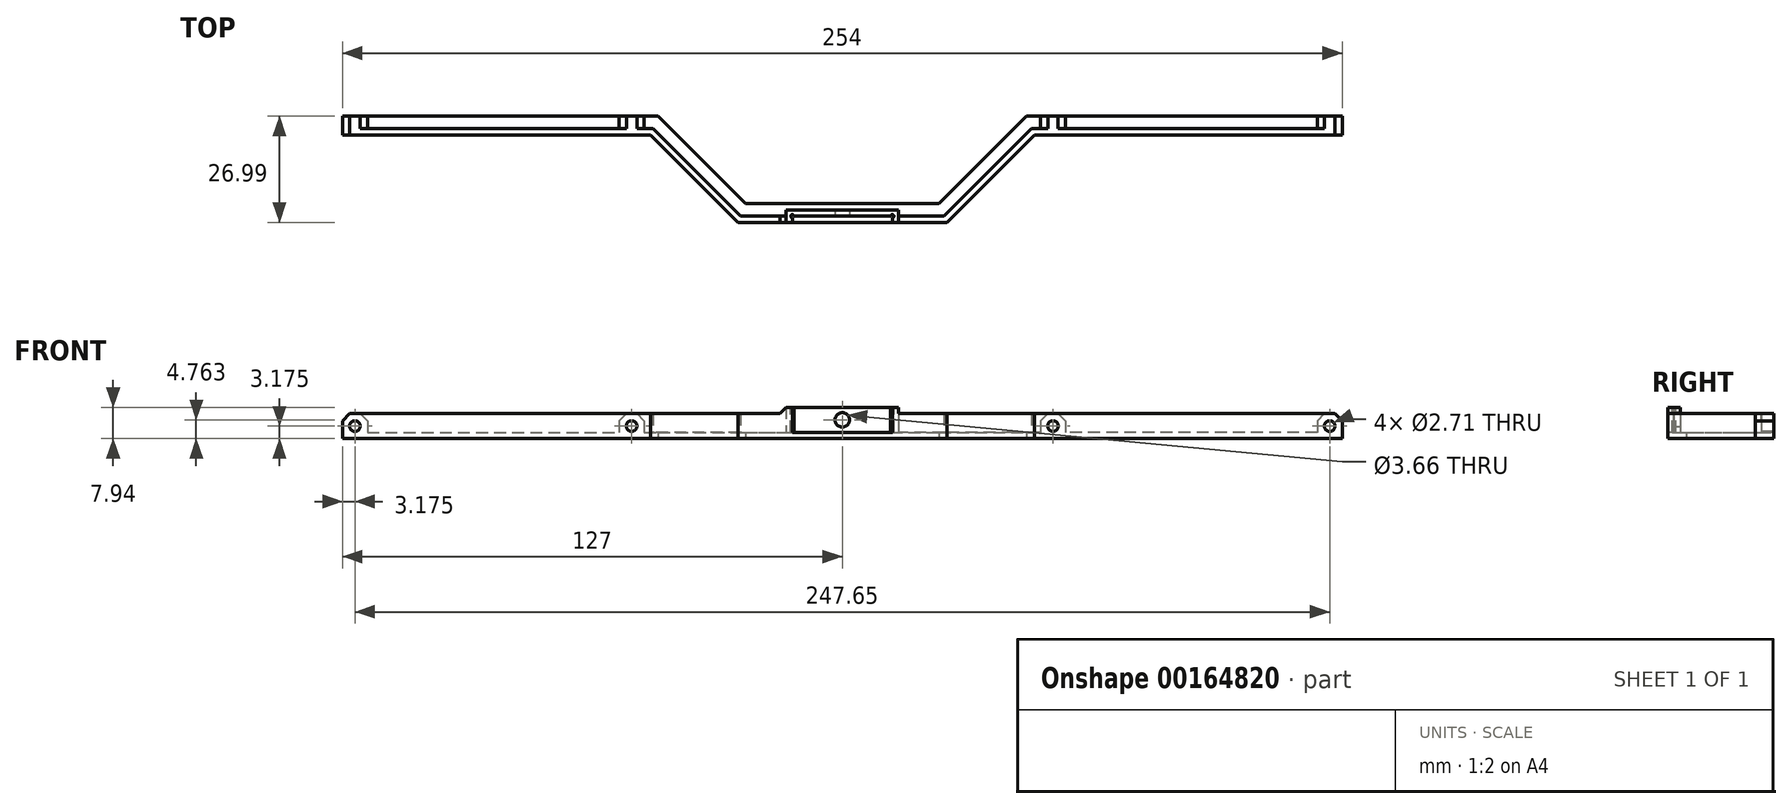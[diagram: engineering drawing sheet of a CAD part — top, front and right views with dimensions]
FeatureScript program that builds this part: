
annotation { "Feature Type Name" : "Feature", "Feature Type Description" : "" }
export const myFeature = defineFeature(function(context is Context, id is Id, definition is map)
    precondition{}
    {
        {
            var Q0;
            Q0=qCreatedBy(makeId("Top.planeOp"),FACE);
            var sketch = newSketch(context, id + "F0", { "sketchPlane" : qUnion([Q0])});
            skLineSegment(sketch, "E0", {"start": v(-127, 22.22) * mm, "end": v(-46.78, 22.22) * mm});
            skLineSegment(sketch, "E1", {"start": v(-46.78, 22.23) * mm, "end": v(-24.56, 0) * mm});
            skLineSegment(sketch, "E2", {"start": v(-24.56, 0) * mm, "end": v(24.56, 0) * mm});
            skLineSegment(sketch, "E3", {"start": v(24.56, 0) * mm, "end": v(46.78, 22.23) * mm});
            skLineSegment(sketch, "E4", {"start": v(46.78, 22.22) * mm, "end": v(127, 22.22) * mm});
            skLineSegment(sketch, "E5", {"start": v(-127, 22.23) * mm, "end": v(-127, 17.46) * mm});
            skLineSegment(sketch, "E6", {"start": v(-127, 17.46) * mm, "end": v(-48.76, 17.46) * mm});
            skLineSegment(sketch, "E7", {"start": v(-48.76, 17.46) * mm, "end": v(-26.53, -4.76) * mm});
            skLineSegment(sketch, "E8", {"start": v(-26.53, -4.76) * mm, "end": v(26.53, -4.76) * mm});
            skLineSegment(sketch, "E9", {"start": v(26.53, -4.76) * mm, "end": v(48.76, 17.46) * mm});
            skLineSegment(sketch, "E10", {"start": v(48.76, 17.46) * mm, "end": v(127, 17.46) * mm});
            skLineSegment(sketch, "E11", {"start": v(127, 17.46) * mm, "end": v(127, 22.23) * mm});
            skLineSegment(sketch, "E12", {"start": v(-35.67, 11.11) * mm, "end": v(-39.04, 7.74) * mm, "construction": true});
            skLineSegment(sketch, "E13", {"start": v(0, 0) * mm, "end": v(0, -4.76) * mm, "construction": true});
            skLineSegment(sketch, "E14", {"start": v(35.67, 11.11) * mm, "end": v(39.04, 7.74) * mm, "construction": true});
            skLineSegment(sketch, "E15", {"start": v(-46.78, 22.22) * mm, "end": v(46.78, 22.22) * mm, "construction": true});
            skLineSegment(sketch, "E16", {"start": v(0, 0) * mm, "end": v(0, 22.22) * mm, "construction": true});
            skSolve(sketch);
        }
        {
            var Q0;
            Q0 = qSketchRegion(id + "F0", true);
            extrude(context, id + "F1", {"entities" : qUnion([Q0]), "depth" : 1.59 * mm});
        }
        {
            var Q0;
            Q0=makeQuery(id+"F1.opExtrude","CAP_FACE",FACE,{"disambiguationData":[OSD([sQuery(id+"F0.wireOp",EDGE,"E0"),sQuery(id+"F0.wireOp",EDGE,"E1"),sQuery(id+"F0.wireOp",EDGE,"E2"),sQuery(id+"F0.wireOp",EDGE,"E3"),sQuery(id+"F0.wireOp",EDGE,"E4"),sQuery(id+"F0.wireOp",EDGE,"E5"),sQuery(id+"F0.wireOp",EDGE,"E6"),sQuery(id+"F0.wireOp",EDGE,"E7"),sQuery(id+"F0.wireOp",EDGE,"E8"),sQuery(id+"F0.wireOp",EDGE,"E9"),sQuery(id+"F0.wireOp",EDGE,"E10"),sQuery(id+"F0.wireOp",EDGE,"E11")])],"isStart":false});
            var sketch = newSketch(context, id + "F2", { "sketchPlane" : qUnion([Q0])});
            skLineSegment(sketch, "E17.bottom", {"start": v(-127, 17.46) * mm, "end": v(-48.76, 17.46) * mm});
            skLineSegment(sketch, "E17.top", {"start": v(-127, 19.05) * mm, "end": v(-48.1, 19.05) * mm});
            skLineSegment(sketch, "E17.left", {"start": v(-127, 17.46) * mm, "end": v(-127, 19.05) * mm});
            skLineSegment(sketch, "E18", {"start": v(-48.76, 17.46) * mm, "end": v(-26.53, -4.76) * mm});
            skLineSegment(sketch, "E19", {"start": v(-26.53, -4.76) * mm, "end": v(26.53, -4.76) * mm});
            skLineSegment(sketch, "E20", {"start": v(26.53, -4.76) * mm, "end": v(48.76, 17.46) * mm});
            skLineSegment(sketch, "E21", {"start": v(48.76, 17.46) * mm, "end": v(127, 17.46) * mm});
            skLineSegment(sketch, "E22", {"start": v(127, 17.46) * mm, "end": v(127, 19.05) * mm});
            skLineSegment(sketch, "E23", {"start": v(127, 19.05) * mm, "end": v(48.1, 19.05) * mm});
            skLineSegment(sketch, "E24", {"start": v(48.1, 19.05) * mm, "end": v(25.87, -3.17) * mm});
            skLineSegment(sketch, "E25", {"start": v(-25.87, -3.18) * mm, "end": v(-48.1, 19.05) * mm});
            skLineSegment(sketch, "E26", {"start": v(-37.64, 6.35) * mm, "end": v(-36.52, 7.47) * mm, "construction": true});
            skLineSegment(sketch, "E27", {"start": v(37.64, 6.35) * mm, "end": v(36.52, 7.47) * mm, "construction": true});
            skLineSegment(sketch, "E28", {"start": v(0, -3.18) * mm, "end": v(0, -4.76) * mm, "construction": true});
            skLineSegment(sketch, "E29", {"start": v(-25.87, -3.18) * mm, "end": v(-14.29, -3.18) * mm});
            skLineSegment(sketch, "E30", {"start": v(25.87, -3.17) * mm, "end": v(14.29, -3.17) * mm});
            skLineSegment(sketch, "E31.bottom", {"start": v(-14.29, -3.18) * mm, "end": v(14.29, -3.18) * mm, "construction": true});
            skLineSegment(sketch, "E31.top", {"start": v(-14.29, -1.59) * mm, "end": v(14.29, -1.59) * mm});
            skLineSegment(sketch, "E31.left", {"start": v(-14.29, -3.18) * mm, "end": v(-14.29, -1.59) * mm});
            skLineSegment(sketch, "E31.right", {"start": v(14.29, -3.18) * mm, "end": v(14.29, -1.59) * mm});
            skSolve(sketch);
        }
        {
            var Q0;
            Q0 = qSketchRegion(id + "F2", true);
            extrude(context, id + "F3", {"entities" : qUnion([Q0]), "operationType" : NewBodyOperationType.ADD, "depth" : 4.76 * mm});
        }
        {
            var Q0;
            Q0=makeQuery(id+"F3.opExtrude","SWEPT_FACE",FACE,{"disambiguationData":[OSD([sQuery(id+"F2.wireOp",EDGE,"E17.top")])]});
            var sketch = newSketch(context, id + "F4", { "sketchPlane" : qUnion([Q0])});
            skLineSegment(sketch, "E32.bottom", {"start": v(-50.34, 6.35) * mm, "end": v(-56.7, 6.35) * mm});
            skLineSegment(sketch, "E32.top", {"start": v(-50.34, 0) * mm, "end": v(-56.7, 0) * mm});
            skLineSegment(sketch, "E32.left", {"start": v(-50.34, 6.35) * mm, "end": v(-50.34, 0) * mm});
            skLineSegment(sketch, "E32.right", {"start": v(-56.7, 6.35) * mm, "end": v(-56.7, 0) * mm});
            skLineSegment(sketch, "E33", {"start": v(-50.34, 3.18) * mm, "end": v(-48.76, 3.18) * mm, "construction": true});
            skLineSegment(sketch, "E34.bottom", {"start": v(-127, 6.35) * mm, "end": v(-120.65, 6.35) * mm});
            skLineSegment(sketch, "E34.top", {"start": v(-127, 0) * mm, "end": v(-120.65, 0) * mm});
            skLineSegment(sketch, "E34.left", {"start": v(-127, 6.35) * mm, "end": v(-127, 0) * mm});
            skLineSegment(sketch, "E34.right", {"start": v(-120.65, 6.35) * mm, "end": v(-120.65, 0) * mm});
            skLineSegment(sketch, "E35.bottom", {"start": v(127, 6.35) * mm, "end": v(120.65, 6.35) * mm});
            skLineSegment(sketch, "E35.top", {"start": v(127, 0) * mm, "end": v(120.65, 0) * mm});
            skLineSegment(sketch, "E35.left", {"start": v(127, 6.35) * mm, "end": v(127, 0) * mm});
            skLineSegment(sketch, "E35.right", {"start": v(120.65, 6.35) * mm, "end": v(120.65, 0) * mm});
            skLineSegment(sketch, "E36.bottom", {"start": v(50.34, 6.35) * mm, "end": v(56.7, 6.35) * mm});
            skLineSegment(sketch, "E36.top", {"start": v(50.34, 0) * mm, "end": v(56.7, 0) * mm});
            skLineSegment(sketch, "E36.left", {"start": v(50.34, 6.35) * mm, "end": v(50.34, 0) * mm});
            skLineSegment(sketch, "E36.right", {"start": v(56.7, 6.35) * mm, "end": v(56.7, 0) * mm});
            skLineSegment(sketch, "E37", {"start": v(120.65, 3.18) * mm, "end": v(56.7, 3.18) * mm, "construction": true});
            skLineSegment(sketch, "E38", {"start": v(-56.7, 3.18) * mm, "end": v(-120.65, 3.17) * mm, "construction": true});
            skSolve(sketch);
        }
        {
            var Q0;
            Q0 = qSketchRegion(id + "F4", true);
            var Q1;
            Q1=makeQuery(id+"F1.opExtrude","SWEPT_FACE",FACE,{"disambiguationData":[OSD([sQuery(id+"F0.wireOp",EDGE,"E0")])]});
            extrude(context, id + "F5", {"entities" : qUnion([Q0]), "operationType" : NewBodyOperationType.ADD, "endBound" : BoundingType.UP_TO_SURFACE, "endBoundEntityFace" : qUnion([Q1]), "depth" : 25.4 * mm});
        }
        {
            var Q0;
            Q0=makeQuery(id+"F5.boolean.opBoolean","MERGE",EDGE,{"derivedFrom":[makeQuery(id+"F3.opExtrude","CAP_EDGE",EDGE,{"disambiguationData":[OSD([sQuery(id+"F2.wireOp",EDGE,"E17.left")])],"isStart":false}),makeQuery(id+"F5.opExtrude","SWEPT_EDGE",EDGE,{"disambiguationData":[OSD([sQuery(id+"F4.wireOp",EDGE,"E35.bottom"),sQuery(id+"F4.wireOp",EDGE,"E35.left")])]})]});
            var Q1;
            Q1=makeQuery(id+"F5.opExtrude","SWEPT_EDGE",EDGE,{"disambiguationData":[OSD([sQuery(id+"F2.wireOp",EDGE,"E17.top"),sQuery(id+"F4.wireOp",EDGE,"E35.bottom"),sQuery(id+"F4.wireOp",EDGE,"E35.right")])]});
            var Q2;
            Q2=makeQuery(id+"F5.opExtrude","SWEPT_EDGE",EDGE,{"disambiguationData":[OSD([sQuery(id+"F2.wireOp",EDGE,"E17.top"),sQuery(id+"F4.wireOp",EDGE,"E36.bottom"),sQuery(id+"F4.wireOp",EDGE,"E36.right")])]});
            var Q3;
            Q3=makeQuery(id+"F5.opExtrude","SWEPT_EDGE",EDGE,{"disambiguationData":[OSD([sQuery(id+"F2.wireOp",EDGE,"E17.top"),sQuery(id+"F4.wireOp",EDGE,"E36.bottom"),sQuery(id+"F4.wireOp",EDGE,"E36.left")])]});
            var Q4;
            Q4=makeQuery(id+"F5.opExtrude","SWEPT_EDGE",EDGE,{"disambiguationData":[OSD([sQuery(id+"F4.wireOp",EDGE,"E32.bottom"),sQuery(id+"F4.wireOp",EDGE,"E32.left")])]});
            var Q5;
            Q5=makeQuery(id+"F5.opExtrude","SWEPT_EDGE",EDGE,{"disambiguationData":[OSD([sQuery(id+"F4.wireOp",EDGE,"E32.bottom"),sQuery(id+"F4.wireOp",EDGE,"E32.right")])]});
            var Q6;
            Q6=makeQuery(id+"F5.opExtrude","SWEPT_EDGE",EDGE,{"disambiguationData":[OSD([sQuery(id+"F4.wireOp",EDGE,"E34.bottom"),sQuery(id+"F4.wireOp",EDGE,"E34.right")])]});
            var Q7;
            Q7=makeQuery(id+"F5.boolean.opBoolean","MERGE",EDGE,{"derivedFrom":[makeQuery(id+"F3.opExtrude","CAP_EDGE",EDGE,{"disambiguationData":[OSD([sQuery(id+"F2.wireOp",EDGE,"E22")])],"isStart":false}),makeQuery(id+"F5.opExtrude","SWEPT_EDGE",EDGE,{"disambiguationData":[OSD([sQuery(id+"F4.wireOp",EDGE,"E34.bottom"),sQuery(id+"F4.wireOp",EDGE,"E34.left")])]})]});
            chamfer(context, id + "F6", {"entities" : qUnion([Q0, Q1, Q2, Q3, Q4, Q5, Q6, Q7]), "width" : 1.86 * mm, "tangentPropagation" : true});
        }
        {
            var Q0;
            Q0=makeQuery(id+"F5.boolean.opBoolean","MERGE",FACE,{"derivedFrom":[makeQuery(id+"F3.opExtrude","CAP_FACE",FACE,{"disambiguationData":[OSD([sQuery(id+"F2.wireOp",EDGE,"E17.bottom"),sQuery(id+"F2.wireOp",EDGE,"E17.top"),sQuery(id+"F2.wireOp",EDGE,"E17.left"),sQuery(id+"F2.wireOp",EDGE,"E18"),sQuery(id+"F2.wireOp",EDGE,"E19"),sQuery(id+"F2.wireOp",EDGE,"E20"),sQuery(id+"F2.wireOp",EDGE,"E21"),sQuery(id+"F2.wireOp",EDGE,"E22"),sQuery(id+"F2.wireOp",EDGE,"E23"),sQuery(id+"F2.wireOp",EDGE,"E24"),sQuery(id+"F2.wireOp",EDGE,"E25"),sQuery(id+"F2.wireOp",EDGE,"E29"),sQuery(id+"F2.wireOp",EDGE,"E30"),sQuery(id+"F2.wireOp",EDGE,"E31.top"),sQuery(id+"F2.wireOp",EDGE,"E31.left"),sQuery(id+"F2.wireOp",EDGE,"E31.right")])],"isStart":false}),makeQuery(id+"F5.opExtrude","SWEPT_FACE",FACE,{"disambiguationData":[OSD([sQuery(id+"F4.wireOp",EDGE,"E32.bottom")])]}),makeQuery(id+"F5.opExtrude","SWEPT_FACE",FACE,{"disambiguationData":[OSD([sQuery(id+"F4.wireOp",EDGE,"E34.bottom")])]}),makeQuery(id+"F5.opExtrude","SWEPT_FACE",FACE,{"disambiguationData":[OSD([sQuery(id+"F4.wireOp",EDGE,"E35.bottom")])]}),makeQuery(id+"F5.opExtrude","SWEPT_FACE",FACE,{"disambiguationData":[OSD([sQuery(id+"F4.wireOp",EDGE,"E36.bottom")])]})]});
            var sketch = newSketch(context, id + "F7", { "sketchPlane" : qUnion([Q0])});
            skLineSegment(sketch, "E39.bottom", {"start": v(-14.29, -1.59) * mm, "end": v(14.29, -1.59) * mm});
            skLineSegment(sketch, "E39.top", {"start": v(-14.29, -4.76) * mm, "end": v(14.29, -4.76) * mm});
            skLineSegment(sketch, "E39.left", {"start": v(-14.29, -1.59) * mm, "end": v(-14.29, -4.76) * mm});
            skLineSegment(sketch, "E39.right", {"start": v(14.29, -1.59) * mm, "end": v(14.29, -4.76) * mm});
            skSolve(sketch);
        }
        {
            var Q0;
            Q0 = qSketchRegion(id + "F7", true);
            extrude(context, id + "F8", {"entities" : qUnion([Q0]), "operationType" : NewBodyOperationType.ADD, "depth" : 1.59 * mm});
        }
        {
            var Q0;
            Q0=makeQuery(id+"F8.opExtrude","CAP_FACE",FACE,{"disambiguationData":[OSD([sQuery(id+"F7.wireOp",EDGE,"E39.bottom"),sQuery(id+"F7.wireOp",EDGE,"E39.top"),sQuery(id+"F7.wireOp",EDGE,"E39.left"),sQuery(id+"F7.wireOp",EDGE,"E39.right")])],"isStart":false});
            var sketch = newSketch(context, id + "F9", { "sketchPlane" : qUnion([Q0])});
            skLineSegment(sketch, "E40.bottom", {"start": v(-12.7, -4.76) * mm, "end": v(12.7, -4.76) * mm});
            skLineSegment(sketch, "E40.top", {"start": v(-12.7, -3.18) * mm, "end": v(12.7, -3.18) * mm});
            skLineSegment(sketch, "E40.left", {"start": v(-12.7, -4.76) * mm, "end": v(-12.7, -3.18) * mm});
            skLineSegment(sketch, "E40.right", {"start": v(12.7, -4.76) * mm, "end": v(12.7, -3.18) * mm});
            skLineSegment(sketch, "E41.bottom", {"start": v(-12.7, -3.18) * mm, "end": v(-14.29, -3.18) * mm, "construction": true});
            skLineSegment(sketch, "E41.top", {"start": v(-12.7, -1.59) * mm, "end": v(-14.29, -1.59) * mm, "construction": true});
            skLineSegment(sketch, "E41.left", {"start": v(-12.7, -3.18) * mm, "end": v(-12.7, -1.59) * mm, "construction": true});
            skLineSegment(sketch, "E41.right", {"start": v(-14.29, -3.18) * mm, "end": v(-14.29, -1.59) * mm, "construction": true});
            skLineSegment(sketch, "E42.bottom", {"start": v(12.7, -3.18) * mm, "end": v(14.29, -3.18) * mm, "construction": true});
            skLineSegment(sketch, "E42.top", {"start": v(12.7, -1.59) * mm, "end": v(14.29, -1.59) * mm, "construction": true});
            skLineSegment(sketch, "E42.left", {"start": v(12.7, -3.18) * mm, "end": v(12.7, -1.59) * mm, "construction": true});
            skLineSegment(sketch, "E42.right", {"start": v(14.29, -3.18) * mm, "end": v(14.29, -1.59) * mm, "construction": true});
            skSolve(sketch);
        }
        {
            var Q0;
            Q0 = qSketchRegion(id + "F9", true);
            var Q1;
            {var subQ0=sQuery(id+"F0.wireOp",EDGE,"E0");var subQ1=sQuery(id+"F0.wireOp",EDGE,"E4");var subQ3=sQuery(id+"F0.wireOp",EDGE,"E1");var subQ4=sQuery(id+"F0.wireOp",EDGE,"E2");var subQ5=sQuery(id+"F0.wireOp",EDGE,"E3");Q1=makeQuery(id+"F5.boolean.opBoolean","SPLIT",FACE,{"disambiguationData":[TD([makeQuery(id+"F1.opExtrude","SWEPT_FACE",FACE,{"disambiguationData":[OSD([subQ3])]})])],"derivedFrom":makeQuery(id+"F1.opExtrude","CAP_FACE",FACE,{"disambiguationData":[OSD([subQ0,subQ3,subQ4,subQ5,subQ1,sQuery(id+"F0.wireOp",EDGE,"E5"),sQuery(id+"F0.wireOp",EDGE,"E6"),sQuery(id+"F0.wireOp",EDGE,"E7"),sQuery(id+"F0.wireOp",EDGE,"E8"),sQuery(id+"F0.wireOp",EDGE,"E9"),sQuery(id+"F0.wireOp",EDGE,"E10"),sQuery(id+"F0.wireOp",EDGE,"E11")])],"isStart":false})});}
            extrude(context, id + "F10", {"entities" : qUnion([Q0]), "operationType" : NewBodyOperationType.REMOVE, "endBound" : BoundingType.UP_TO_SURFACE, "oppositeDirection" : true, "endBoundEntityFace" : qUnion([Q1]), "depth" : 25.4 * mm});
        }
        {
            var Q0;
            Q0=makeQuery(id+"F8.opExtrude","CAP_EDGE",EDGE,{"disambiguationData":[OSD([sQuery(id+"F7.wireOp",EDGE,"E39.left")])],"isStart":true});
            var Q1;
            Q1=makeQuery(id+"F8.opExtrude","CAP_EDGE",EDGE,{"disambiguationData":[OSD([sQuery(id+"F7.wireOp",EDGE,"E39.right")])],"isStart":true});
            chamfer(context, id + "F11", {"entities" : qUnion([Q0, Q1]), "width" : 1.59 * mm, "tangentPropagation" : true});
        }
        {
            var Q0;
            Q0=makeQuery(id+"F10.boolean.opBoolean","COPY",FACE,{"derivedFrom":makeQuery(id+"F10.opExtrude","SWEPT_FACE",FACE,{"disambiguationData":[OSD([sQuery(id+"F9.wireOp",EDGE,"E40.top")])]})});
            var sketch = newSketch(context, id + "F12", { "sketchPlane" : qUnion([Q0])});
            skLineSegment(sketch, "E43", {"start": v(123.82, 6.35) * mm, "end": v(123.82, 0) * mm, "construction": true});
            skLineSegment(sketch, "E44", {"start": v(53.52, 6.35) * mm, "end": v(53.52, 0) * mm, "construction": true});
            skCircle(sketch, "E45", {"center": v(53.52, 3.18) * mm, "radius": 1.35 * mm});
            skCircle(sketch, "E46", {"center": v(123.82, 3.18) * mm, "radius": 1.35 * mm});
            skLineSegment(sketch, "E47", {"start": v(-53.52, 6.35) * mm, "end": v(-53.52, 0) * mm, "construction": true});
            skLineSegment(sketch, "E48", {"start": v(-123.83, 6.35) * mm, "end": v(-123.83, 0) * mm, "construction": true});
            skCircle(sketch, "E49", {"center": v(-123.83, 3.18) * mm, "radius": 1.35 * mm});
            skCircle(sketch, "E50", {"center": v(-53.52, 3.18) * mm, "radius": 1.35 * mm});
            skLineSegment(sketch, "E51", {"start": v(0, 7.94) * mm, "end": v(0, 1.59) * mm, "construction": true});
            skCircle(sketch, "E52", {"center": v(0, 4.76) * mm, "radius": 1.83 * mm});
            skSolve(sketch);
        }
        {
            var Q0;
            Q0 = qSketchRegion(id + "F12", true);
            var Q1;
            {var subQ0=sQuery(id+"F0.wireOp",EDGE,"E0");Q1=makeQuery(id+"F5.boolean.opBoolean","MERGE",FACE,{"derivedFrom":[makeQuery(id+"F1.opExtrude","SWEPT_FACE",FACE,{"disambiguationData":[OSD([subQ0])]}),makeQuery(id+"F5.opExtrude","CAP_FACE",FACE,{"disambiguationData":[OSD([subQ0]),ownerDisambiguation([makeQuery(id+"F5.opExtrude","SWEPT_BODY",BODY,{"disambiguationData":[OSD([sQuery(id+"F4.wireOp",EDGE,"E35.bottom"),sQuery(id+"F4.wireOp",EDGE,"E35.top"),sQuery(id+"F4.wireOp",EDGE,"E35.left"),sQuery(id+"F4.wireOp",EDGE,"E35.right")])]})])],"isStart":false}),makeQuery(id+"F5.opExtrude","CAP_FACE",FACE,{"disambiguationData":[OSD([subQ0]),ownerDisambiguation([makeQuery(id+"F5.opExtrude","SWEPT_BODY",BODY,{"disambiguationData":[OSD([sQuery(id+"F4.wireOp",EDGE,"E36.bottom"),sQuery(id+"F4.wireOp",EDGE,"E36.top"),sQuery(id+"F4.wireOp",EDGE,"E36.left"),sQuery(id+"F4.wireOp",EDGE,"E36.right")])]})])],"isStart":false})]});}
            extrude(context, id + "F13", {"entities" : qUnion([Q0]), "operationType" : NewBodyOperationType.REMOVE, "endBound" : BoundingType.UP_TO_SURFACE, "oppositeDirection" : true, "endBoundEntityFace" : qUnion([Q1]), "depth" : 25.4 * mm});
        }
        {
            var Q0;
            Q0=makeQuery(id+"F8.opExtrude","CAP_FACE",FACE,{"disambiguationData":[OSD([sQuery(id+"F7.wireOp",EDGE,"E39.bottom"),sQuery(id+"F7.wireOp",EDGE,"E39.top"),sQuery(id+"F7.wireOp",EDGE,"E39.left"),sQuery(id+"F7.wireOp",EDGE,"E39.right")])],"isStart":false});
            var sketch = newSketch(context, id + "F14", { "sketchPlane" : qUnion([Q0])});
            skCircle(sketch, "E53", {"center": v(12.7, -3.18) * mm, "radius": 0.4 * mm});
            skCircle(sketch, "E54", {"center": v(-12.7, -3.18) * mm, "radius": 0.4 * mm});
            skSolve(sketch);
        }
        {
            var Q0;
            Q0 = qSketchRegion(id + "F14", true);
            var Q1;
            Q1=makeQuery(id+"F10.boolean.opBoolean","COPY",FACE,{"derivedFrom":makeQuery(id+"F10.opExtrude","CAP_FACE",FACE,{"disambiguationData":[OSD([sQuery(id+"F9.wireOp",EDGE,"E40.bottom"),sQuery(id+"F9.wireOp",EDGE,"E40.top"),sQuery(id+"F9.wireOp",EDGE,"E40.left"),sQuery(id+"F9.wireOp",EDGE,"E40.right")])],"isStart":false})});
            extrude(context, id + "F15", {"entities" : qUnion([Q0]), "operationType" : NewBodyOperationType.REMOVE, "endBound" : BoundingType.UP_TO_SURFACE, "oppositeDirection" : true, "endBoundEntityFace" : qUnion([Q1]), "depth" : 25.4 * mm});
        }
    });
